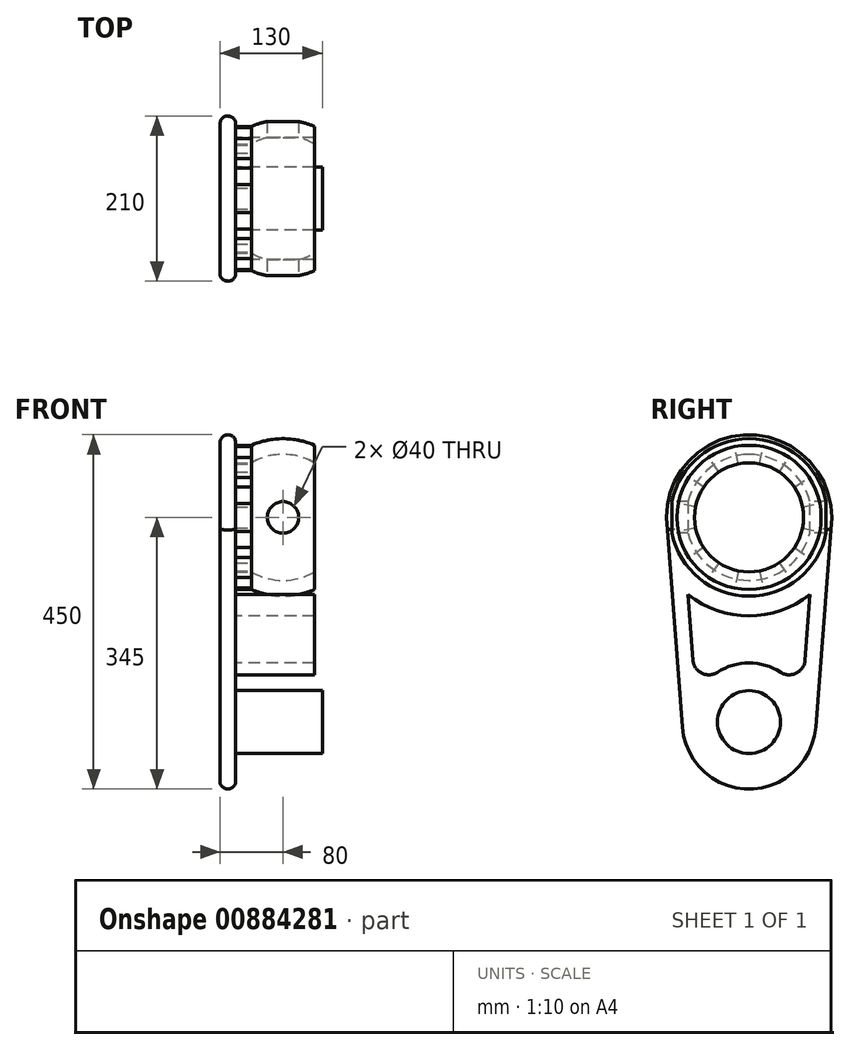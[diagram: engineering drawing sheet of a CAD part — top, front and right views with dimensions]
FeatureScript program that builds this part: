
annotation { "Feature Type Name" : "Feature", "Feature Type Description" : "" }
export const myFeature = defineFeature(function(context is Context, id is Id, definition is map)
    precondition{}
    {
        {
            var Q0;
            Q0=qCreatedBy(makeId("Front.planeOp"),FACE);
            var sketch = newSketch(context, id + "F0", { "sketchPlane" : qUnion([Q0])});
            skLineSegment(sketch, "E0", {"start": v(0, 0) * mm, "end": v(154.67, 0) * mm, "construction": true});
            skLineSegment(sketch, "E1", {"start": v(40, 91.65) * mm, "end": v(40, 69.28) * mm});
            skLineSegment(sketch, "E2", {"start": v(-40, 91.65) * mm, "end": v(-40, 69.28) * mm});
            skArc(sketch, "E3", {"start": v(40, 69.28) * mm, "mid": v(0, 80) * mm, "end": v(-40, 69.28) * mm});
            skLineSegment(sketch, "E4", {"start": v(0, 2.73) * mm, "end": v(0, 112.94) * mm, "construction": true});
            skArc(sketch, "E5", {"start": v(40, 91.65) * mm, "mid": v(0, 100) * mm, "end": v(-40, 91.65) * mm});
            skSolve(sketch);
        }
        {
            var Q0;
            Q0=makeQuery(id+"F0.imprint","IMPRINT",FACE,{"disambiguationData":[TD([[makeQuery(id+"F0.imprint","IMPRINT",EDGE,{"derivedFrom":sQuery(id+"F0.wireOp",EDGE,"E1")}),-1.0]])]});
            var Q1;
            Q1=sQuery(id+"F0.wireOp",EDGE,"E0");
            revolve(context, id + "F1", {"surfaceOperationType" : NewSurfaceOperationType.NEW, "entities" : qUnion([Q0]), "axis" : qUnion([Q1]), "revolveType" : RevolveType.FULL});
        }
        {
            var Q0;
            Q0=qCreatedBy(makeId("Front.planeOp"),FACE);
            var sketch = newSketch(context, id + "F2", { "sketchPlane" : qUnion([Q0])});
            skCircle(sketch, "E6", {"center": v(0, 0) * mm, "radius": 20 * mm});
            skSolve(sketch);
        }
        {
            var Q0;
            Q0 = qSketchRegion(id + "F2", true);
            extrude(context, id + "F3", {"entities" : qUnion([Q0]), "operationType" : NewBodyOperationType.REMOVE, "endBound" : BoundingType.THROUGH_ALL, "oppositeDirection" : true, "depth" : 25 * mm, "offsetDistance" : 25 * mm, "hasSecondDirection" : true, "secondDirectionBound" : SecondDirectionBoundingType.THROUGH_ALL, "secondDirectionOppositeDirection" : false, "secondDirectionDepth" : 25 * mm});
        }
        {
            var Q0;
            Q0=makeQuery(id+"F1.opRevolve","SWEPT_FACE",FACE,{"disambiguationData":[OSD([sQuery(id+"F0.wireOp",EDGE,"E2")])]});
            var sketch = newSketch(context, id + "F4", { "sketchPlane" : qUnion([Q0])});
            skLineSegment(sketch, "E7", {"start": v(0, 69.28) * mm, "end": v(0, 91.65) * mm});
            skLineSegment(sketch, "E8.1.0", {"start": v(-13.52, 67.95) * mm, "end": v(-17.88, 89.9) * mm});
            skLineSegment(sketch, "E8.3.0", {"start": v(-38.5, 57.6) * mm, "end": v(-50.92, 76.2) * mm});
            skLineSegment(sketch, "E8.5.0", {"start": v(-57.6, 38.5) * mm, "end": v(-76.2, 50.92) * mm});
            skLineSegment(sketch, "E8.7.0", {"start": v(-67.95, 13.52) * mm, "end": v(-89.9, 17.88) * mm});
            skLineSegment(sketch, "E8.9.0", {"start": v(-67.95, -13.52) * mm, "end": v(-89.9, -17.88) * mm});
            skLineSegment(sketch, "E8.11.0", {"start": v(-57.6, -38.5) * mm, "end": v(-76.2, -50.92) * mm});
            skLineSegment(sketch, "E8.13.0", {"start": v(-38.5, -57.6) * mm, "end": v(-50.92, -76.2) * mm});
            skLineSegment(sketch, "E8.15.0", {"start": v(-13.52, -67.95) * mm, "end": v(-17.88, -89.9) * mm});
            skLineSegment(sketch, "E8.17.0", {"start": v(13.52, -67.95) * mm, "end": v(17.88, -89.9) * mm});
            skLineSegment(sketch, "E8.19.0", {"start": v(38.5, -57.6) * mm, "end": v(50.92, -76.2) * mm});
            skLineSegment(sketch, "E8.21.0", {"start": v(57.6, -38.5) * mm, "end": v(76.2, -50.92) * mm});
            skLineSegment(sketch, "E8.23.0", {"start": v(67.95, -13.52) * mm, "end": v(89.9, -17.88) * mm});
            skLineSegment(sketch, "E8.25.0", {"start": v(67.95, 13.52) * mm, "end": v(89.9, 17.88) * mm});
            skLineSegment(sketch, "E8.27.0", {"start": v(57.6, 38.5) * mm, "end": v(76.2, 50.92) * mm});
            skLineSegment(sketch, "E8.29.0", {"start": v(38.5, 57.6) * mm, "end": v(50.92, 76.2) * mm});
            skLineSegment(sketch, "E8.31.0", {"start": v(13.52, 67.95) * mm, "end": v(17.88, 89.9) * mm});
            skPoint(sketch, "E8.center", {"position": v(0, 0) * mm});
            skArc(sketch, "E9", {"start": v(-38.5, 57.6) * mm, "mid": v(-48.99, 48.99) * mm, "end": v(-57.6, 38.5) * mm});
            skArc(sketch, "E10", {"start": v(-50.92, 76.2) * mm, "mid": v(-64.8, 64.8) * mm, "end": v(-76.2, 50.92) * mm});
            skArc(sketch, "E11.trimOffspring", {"start": v(-67.95, 13.52) * mm, "mid": v(-69.28, 0) * mm, "end": v(-67.95, -13.52) * mm});
            skArc(sketch, "E12.trimOffspring", {"start": v(-89.9, 17.88) * mm, "mid": v(-91.65, 0) * mm, "end": v(-89.9, -17.88) * mm});
            skArc(sketch, "E13.trimOffspring", {"start": v(-57.6, -38.5) * mm, "mid": v(-48.99, -48.99) * mm, "end": v(-38.5, -57.6) * mm});
            skArc(sketch, "E14.trimOffspring", {"start": v(-76.2, -50.92) * mm, "mid": v(-64.8, -64.8) * mm, "end": v(-50.92, -76.2) * mm});
            skArc(sketch, "E15.trimOffspring", {"start": v(-17.88, -89.9) * mm, "mid": v(0, -91.65) * mm, "end": v(17.88, -89.9) * mm});
            skArc(sketch, "E16.trimOffspring", {"start": v(-13.52, -67.95) * mm, "mid": v(0, -69.28) * mm, "end": v(13.52, -67.95) * mm});
            skArc(sketch, "E17.trimOffspring", {"start": v(50.92, -76.2) * mm, "mid": v(64.8, -64.8) * mm, "end": v(76.2, -50.92) * mm});
            skArc(sketch, "E18.trimOffspring", {"start": v(38.5, -57.6) * mm, "mid": v(48.99, -48.99) * mm, "end": v(57.6, -38.5) * mm});
            skArc(sketch, "E19.trimOffspring", {"start": v(89.9, -17.88) * mm, "mid": v(91.65, 0) * mm, "end": v(89.9, 17.88) * mm});
            skArc(sketch, "E20.trimOffspring", {"start": v(67.95, -13.52) * mm, "mid": v(68.95, -6.8) * mm, "end": v(69.28, 0) * mm});
            skArc(sketch, "E21.trimOffspring", {"start": v(76.2, 50.92) * mm, "mid": v(64.8, 64.8) * mm, "end": v(50.92, 76.2) * mm});
            skArc(sketch, "E22.trimOffspring", {"start": v(57.6, 38.5) * mm, "mid": v(48.99, 48.99) * mm, "end": v(38.5, 57.6) * mm});
            skArc(sketch, "E23.trimOffspring", {"start": v(13.52, 67.95) * mm, "mid": v(0, 69.28) * mm, "end": v(-13.52, 67.95) * mm});
            skArc(sketch, "E24.trimOffspring", {"start": v(17.88, 89.9) * mm, "mid": v(0, 91.65) * mm, "end": v(-17.88, 89.9) * mm});
            skSolve(sketch);
        }
        {
            var Q0;
            {var subQ0=sQuery(id+"F4.wireOp",EDGE,"E7");Q0=makeQuery(id+"F4.imprint","IMPRINT",FACE,{"disambiguationData":[TD([[makeQuery(id+"F4.imprint","IMPRINT",EDGE,{"derivedFrom":subQ0}),-1.0]])]});}
            var Q1;
            Q1=makeQuery(id+"F4.imprint","IMPRINT",FACE,{"disambiguationData":[TD([[makeQuery(id+"F4.imprint","IMPRINT",EDGE,{"derivedFrom":sQuery(id+"F4.wireOp",EDGE,"E8.3.0")}),1.0]])]});
            var Q2;
            Q2=makeQuery(id+"F4.imprint","IMPRINT",FACE,{"disambiguationData":[TD([[makeQuery(id+"F4.imprint","IMPRINT",EDGE,{"derivedFrom":sQuery(id+"F4.wireOp",EDGE,"E8.7.0")}),1.0]])]});
            var Q3;
            Q3=makeQuery(id+"F4.imprint","IMPRINT",FACE,{"disambiguationData":[TD([[makeQuery(id+"F4.imprint","IMPRINT",EDGE,{"derivedFrom":sQuery(id+"F4.wireOp",EDGE,"E8.11.0")}),1.0]])]});
            var Q4;
            Q4=makeQuery(id+"F4.imprint","IMPRINT",FACE,{"disambiguationData":[TD([[makeQuery(id+"F4.imprint","IMPRINT",EDGE,{"derivedFrom":sQuery(id+"F4.wireOp",EDGE,"E8.15.0")}),1.0]])]});
            var Q5;
            Q5=makeQuery(id+"F4.imprint","IMPRINT",FACE,{"disambiguationData":[TD([[makeQuery(id+"F4.imprint","IMPRINT",EDGE,{"derivedFrom":sQuery(id+"F4.wireOp",EDGE,"E8.19.0")}),1.0]])]});
            var Q6;
            Q6=makeQuery(id+"F4.imprint","IMPRINT",FACE,{"disambiguationData":[TD([[makeQuery(id+"F4.imprint","IMPRINT",EDGE,{"derivedFrom":sQuery(id+"F4.wireOp",EDGE,"E8.27.0")}),1.0]])]});
            var Q7;
            {var subQ0=sQuery(id+"F4.wireOp",EDGE,"E7");Q7=makeQuery(id+"F4.imprint","IMPRINT",FACE,{"disambiguationData":[TD([[makeQuery(id+"F4.imprint","IMPRINT",EDGE,{"derivedFrom":subQ0}),1.0]])]});}
            var Q8;
            Q8=makeQuery(id+"F4.imprint","IMPRINT",FACE,{"disambiguationData":[TD([[makeQuery(id+"F4.imprint","IMPRINT",EDGE,{"derivedFrom":sQuery(id+"F4.wireOp",EDGE,"E8.23.0")}),1.0]])]});
            extrude(context, id + "F5", {"entities" : qUnion([Q0, Q1, Q2, Q3, Q4, Q5, Q6, Q7, Q8]), "operationType" : NewBodyOperationType.ADD, "depth" : 20 * mm, "offsetDistance" : 25 * mm});
        }
        {
            var Q0;
            Q0=makeQuery(id+"F5.opExtrude","CAP_FACE",FACE,{"disambiguationData":[OSD([sQuery(id+"F4.wireOp",EDGE,"E8.1.0"),sQuery(id+"F4.wireOp",EDGE,"E8.31.0"),sQuery(id+"F4.wireOp",EDGE,"E23.trimOffspring"),sQuery(id+"F4.wireOp",EDGE,"E24.trimOffspring")])],"isStart":false});
            var sketch = newSketch(context, id + "F6", { "sketchPlane" : qUnion([Q0])});
            skArc(sketch, "E25", {"start": v(103.8, -15.86) * mm, "mid": v(0, 105) * mm, "end": v(-103.8, -15.86) * mm});
            skLineSegment(sketch, "E26", {"start": v(-105, 0) * mm, "end": v(-84.76, -266.44) * mm});
            skArc(sketch, "E27", {"start": v(-84.76, -266.44) * mm, "mid": v(0, -345) * mm, "end": v(84.76, -266.44) * mm});
            skLineSegment(sketch, "E28", {"start": v(0, 0) * mm, "end": v(0, -260) * mm, "construction": true});
            skLineSegment(sketch, "E29.MirrorCS", {"start": v(105, 0) * mm, "end": v(84.76, -266.44) * mm});
            skSolve(sketch);
        }
        {
            var Q0;
            Q0 = qSketchRegion(id + "F6", true);
            extrude(context, id + "F7", {"entities" : qUnion([Q0]), "operationType" : NewBodyOperationType.ADD, "depth" : 20 * mm, "offsetDistance" : 25 * mm});
        }
        {
            var Q0;
            Q0=makeQuery(id+"F7.opExtrude","CAP_FACE",FACE,{"disambiguationData":[OSD([sQuery(id+"F6.wireOp",EDGE,"E25"),sQuery(id+"F6.wireOp",EDGE,"E26"),sQuery(id+"F6.wireOp",EDGE,"E27"),sQuery(id+"F6.wireOp",EDGE,"E29.MirrorCS")])],"isStart":true});
            var sketch = newSketch(context, id + "F8", { "sketchPlane" : qUnion([Q0])});
            skArc(sketch, "E30", {"start": v(-77.49, -98.08) * mm, "mid": v(0, -125) * mm, "end": v(77.49, -98.08) * mm});
            skLineSegment(sketch, "E31", {"start": v(-77.49, -98.08) * mm, "end": v(-71.15, -181.5) * mm});
            skArc(sketch, "E32", {"start": v(40.43, -196.83) * mm, "mid": v(0, -185) * mm, "end": v(-40.43, -196.83) * mm});
            skLineSegment(sketch, "E33", {"start": v(77.49, -98.08) * mm, "end": v(71.15, -181.5) * mm});
            skPoint(sketch, "E34.visualSharp", {"position": v(67.65, -227.62) * mm});
            skArc(sketch, "E34.filletArc", {"start": v(40.43, -196.83) * mm, "mid": v(60.14, -197.88) * mm, "end": v(71.15, -181.5) * mm});
            skPoint(sketch, "E35.visualSharp", {"position": v(-67.65, -227.62) * mm});
            skArc(sketch, "E35.filletArc", {"start": v(-71.15, -181.5) * mm, "mid": v(-60.14, -197.88) * mm, "end": v(-40.43, -196.83) * mm});
            skSolve(sketch);
        }
        {
            var Q0;
            Q0=makeQuery(id+"F8.imprint","IMPRINT",FACE,{"disambiguationData":[TD([[makeQuery(id+"F8.imprint","IMPRINT",EDGE,{"derivedFrom":sQuery(id+"F8.wireOp",EDGE,"E30")}),-1.0]])]});
            extrude(context, id + "F9", {"entities" : qUnion([Q0]), "operationType" : NewBodyOperationType.ADD, "depth" : 100 * mm, "offsetDistance" : 25 * mm});
        }
        {
            var Q0;
            {var subQ0=sQuery(id+"F6.wireOp",EDGE,"E29.MirrorCS");var subQ1=sQuery(id+"F6.wireOp",EDGE,"E27");var subQ2=sQuery(id+"F6.wireOp",EDGE,"E26");Q0=makeQuery(id+"F9.boolean.opBoolean","SPLIT",FACE,{"disambiguationData":[TD([makeQuery(id+"F7.opExtrude","SWEPT_FACE",FACE,{"disambiguationData":[OSD([subQ1])]})])],"derivedFrom":makeQuery(id+"F7.opExtrude","CAP_FACE",FACE,{"disambiguationData":[OSD([sQuery(id+"F6.wireOp",EDGE,"E25"),subQ2,subQ1,subQ0])],"isStart":true})});}
            var sketch = newSketch(context, id + "F10", { "sketchPlane" : qUnion([Q0])});
            skCircle(sketch, "E36", {"center": v(0, -260) * mm, "radius": 40 * mm});
            skSolve(sketch);
        }
        {
            var Q0;
            Q0 = qSketchRegion(id + "F10", true);
            extrude(context, id + "F11", {"entities" : qUnion([Q0]), "operationType" : NewBodyOperationType.ADD, "depth" : 110 * mm, "offsetDistance" : 25 * mm});
        }
        {
            var Q0;
            Q0=makeQuery(id+"F7.opExtrude","CAP_EDGE",EDGE,{"disambiguationData":[OSD([sQuery(id+"F6.wireOp",EDGE,"E25")])],"isStart":true});
            var Q1;
            Q1=makeQuery(id+"F7.opExtrude","CAP_EDGE",EDGE,{"disambiguationData":[OSD([sQuery(id+"F6.wireOp",EDGE,"E29.MirrorCS")])],"isStart":true});
            var Q2;
            Q2=makeQuery(id+"F7.opExtrude","CAP_EDGE",EDGE,{"disambiguationData":[OSD([sQuery(id+"F6.wireOp",EDGE,"E29.MirrorCS")])],"isStart":false});
            var Q3;
            Q3=makeQuery(id+"F7.opExtrude","CAP_EDGE",EDGE,{"disambiguationData":[OSD([sQuery(id+"F6.wireOp",EDGE,"E25")])],"isStart":false});
            fillet(context, id + "F12", {"entities" : qUnion([Q0, Q1, Q2, Q3]), "radius" : 10 * mm, "tangentPropagation" : true, "allowEdgeOverflow" : false});
        }
    });
